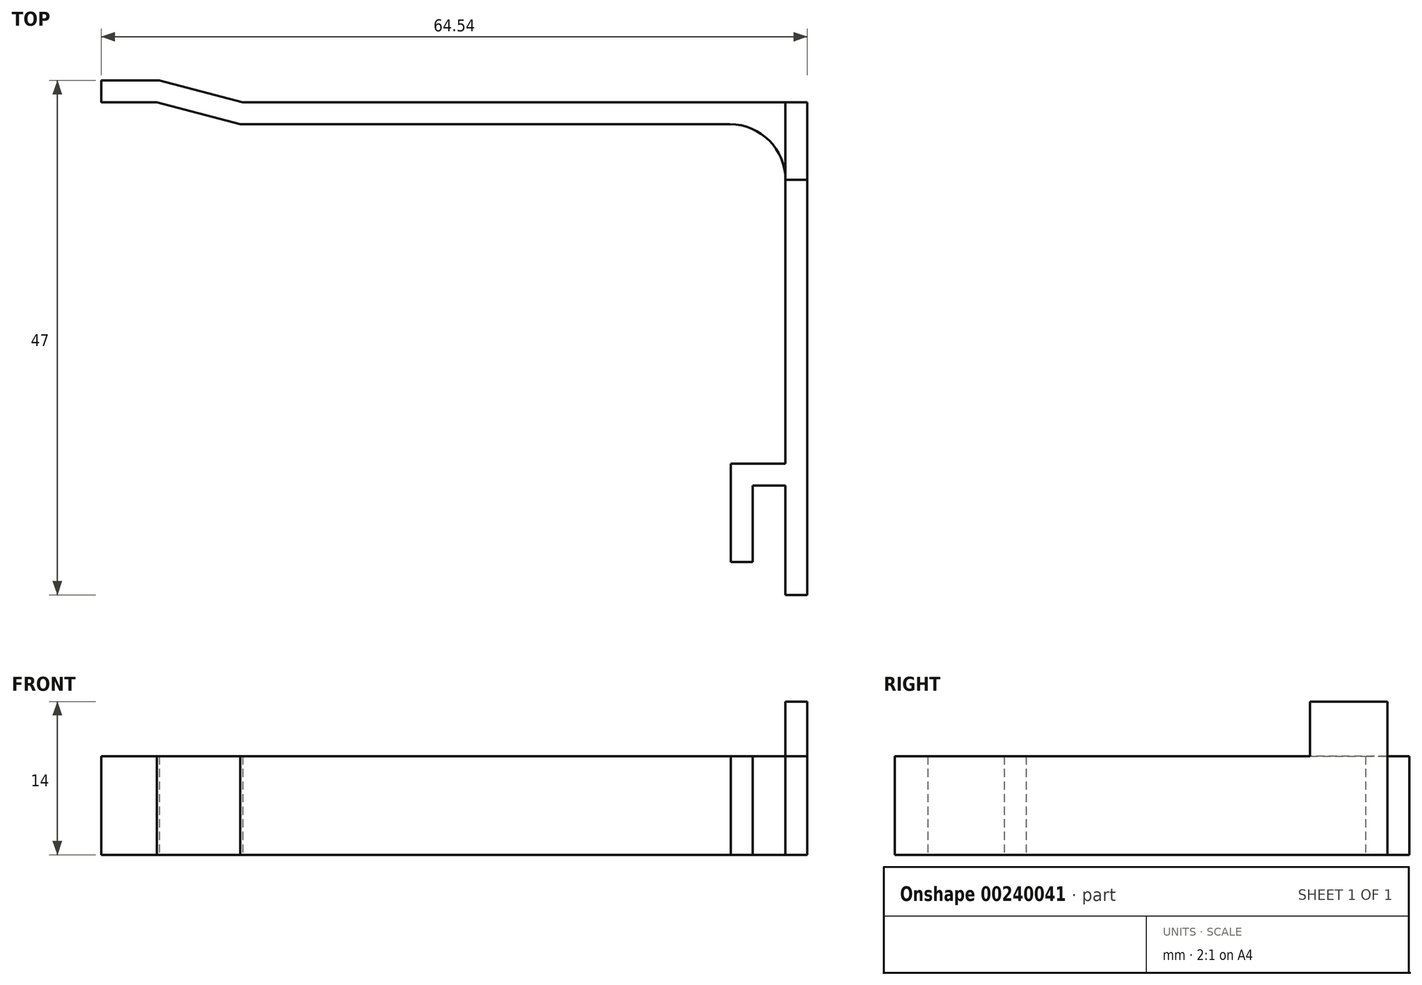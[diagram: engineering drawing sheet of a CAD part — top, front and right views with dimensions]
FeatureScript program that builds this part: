
annotation { "Feature Type Name" : "Feature", "Feature Type Description" : "" }
export const myFeature = defineFeature(function(context is Context, id is Id, definition is map)
    precondition{}
    {
        {
            var Q0;
            Q0=qCreatedBy(makeId("Top.planeOp"),FACE);
            var sketch = newSketch(context, id + "F0", { "sketchPlane" : qUnion([Q0])});
            skLineSegment(sketch, "E0", {"start": v(55, 3) * mm, "end": v(55, 12) * mm});
            skLineSegment(sketch, "E1", {"start": v(55, 12) * mm, "end": v(60, 12) * mm});
            skLineSegment(sketch, "E2", {"start": v(60, 12) * mm, "end": v(60, 37.92) * mm});
            skLineSegment(sketch, "E3", {"start": v(54.92, 43) * mm, "end": v(10.16, 43) * mm});
            skLineSegment(sketch, "E4", {"start": v(10.4, 45) * mm, "end": v(62, 45) * mm});
            skLineSegment(sketch, "E5", {"start": v(62, 45) * mm, "end": v(62, 0) * mm});
            skLineSegment(sketch, "E6", {"start": v(62, 0) * mm, "end": v(60, 0) * mm});
            skLineSegment(sketch, "E7", {"start": v(60, 0) * mm, "end": v(60, 10) * mm});
            skLineSegment(sketch, "E8", {"start": v(60, 10) * mm, "end": v(57, 10) * mm});
            skLineSegment(sketch, "E9", {"start": v(57, 10) * mm, "end": v(57, 3) * mm});
            skLineSegment(sketch, "E10", {"start": v(10.16, 43) * mm, "end": v(2.54, 45) * mm});
            skLineSegment(sketch, "E11", {"start": v(2.54, 45) * mm, "end": v(-2.54, 45) * mm});
            skLineSegment(sketch, "E12", {"start": v(-2.54, 45) * mm, "end": v(-2.54, 47) * mm});
            skLineSegment(sketch, "E13", {"start": v(-2.54, 47) * mm, "end": v(2.78, 47) * mm});
            skLineSegment(sketch, "E14", {"start": v(2.78, 47) * mm, "end": v(10.4, 45) * mm});
            skPoint(sketch, "E15.visualSharp", {"position": v(60, 43) * mm});
            skArc(sketch, "E15.filletArc", {"start": v(60, 37.92) * mm, "mid": v(58.51, 41.51) * mm, "end": v(54.92, 43) * mm});
            skLineSegment(sketch, "E16", {"start": v(55, 3) * mm, "end": v(57, 3) * mm});
            skPoint(sketch, "E17.orphan", {"position": v(57, 0) * mm});
            skSolve(sketch);
        }
        {
            var Q0;
            Q0=makeQuery(id+"F0.imprint","IMPRINT",FACE,{"disambiguationData":[TD([[makeQuery(id+"F0.imprint","IMPRINT",EDGE,{"derivedFrom":sQuery(id+"F0.wireOp",EDGE,"E0")}),-1.0]])]});
            extrude(context, id + "F1", {"entities" : qUnion([Q0]), "depth" : 9 * mm});
        }
        {
            var Q0;
            Q0=makeQuery(id+"F1.opExtrude","CAP_FACE",FACE,{"disambiguationData":[OSD([sQuery(id+"F0.wireOp",EDGE,"E0"),sQuery(id+"F0.wireOp",EDGE,"E1"),sQuery(id+"F0.wireOp",EDGE,"E2"),sQuery(id+"F0.wireOp",EDGE,"E3"),sQuery(id+"F0.wireOp",EDGE,"E4"),sQuery(id+"F0.wireOp",EDGE,"E5"),sQuery(id+"F0.wireOp",EDGE,"E6"),sQuery(id+"F0.wireOp",EDGE,"E7"),sQuery(id+"F0.wireOp",EDGE,"E8"),sQuery(id+"F0.wireOp",EDGE,"E9"),sQuery(id+"F0.wireOp",EDGE,"pSbDqQbU-yhJj-qwMG-qpoE-NNgh6YpPeQvC"),sQuery(id+"F0.wireOp",EDGE,"E10"),sQuery(id+"F0.wireOp",EDGE,"E11"),sQuery(id+"F0.wireOp",EDGE,"E12"),sQuery(id+"F0.wireOp",EDGE,"E13"),sQuery(id+"F0.wireOp",EDGE,"E14"),sQuery(id+"F0.wireOp",EDGE,"E15.filletArc")])],"isStart":false});
            var sketch = newSketch(context, id + "F2", { "sketchPlane" : qUnion([Q0])});
            skLineSegment(sketch, "E18.bottom", {"start": v(62, 45) * mm, "end": v(60, 45) * mm});
            skLineSegment(sketch, "E18.top", {"start": v(62, 37.92) * mm, "end": v(60, 37.92) * mm});
            skLineSegment(sketch, "E18.left", {"start": v(62, 45) * mm, "end": v(62, 37.92) * mm});
            skLineSegment(sketch, "E18.right", {"start": v(60, 45) * mm, "end": v(60, 37.92) * mm});
            skSolve(sketch);
        }
        {
            var Q0;
            Q0=makeQuery(id+"F2.imprint","IMPRINT",FACE,{"disambiguationData":[TD([[makeQuery(id+"F2.imprint","IMPRINT",EDGE,{"derivedFrom":sQuery(id+"F2.wireOp",EDGE,"E18.bottom")}),-1.0]])]});
            extrude(context, id + "F3", {"entities" : qUnion([Q0]), "operationType" : NewBodyOperationType.ADD, "depth" : 5 * mm});
        }
    });
